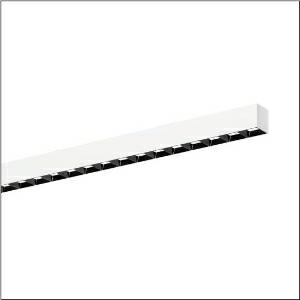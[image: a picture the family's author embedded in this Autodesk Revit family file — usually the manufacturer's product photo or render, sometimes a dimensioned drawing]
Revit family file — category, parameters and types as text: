
# Revit family: silica_r__21_51mx21dc4awb_19b2
name_source: partatom
category: Lighting Fixtures
units: mm (PartAtom-declared; Revit-internal decimal feet)

## family parameters
Cut with Voids When Loaded = No
Host = Face
Light Source = No
Part Type = Normal
Room Calculation Point = No
Round Connector Dimension = Use Diameter
Shared = No

## types (1)
- --- (1 x LED, 10800 lm, 64.8 W, 4000K)
    Apparent Load = 65 VA
    CIE Flux Codes = 87 99 100 100 100
    Color Rendering = 80
    Color Temperature = 4000K
    Default Elevation = 1800 mm
    Description = Silica® 21, office luminaire, primary light control with darklight reflector, of PMMA, black, CAT 2 (L<= 3000cd/m²), light emission: direct distribution, primary light characteristic: symmetric, installation type: surface-mounted, LED, rated luminous flux: 10.800lm, luminous efficacy: 167lm/W, light colour: 840, colour temperature: 4000K, control gear: DALI 2, with terminal, 3+2-pole, max. 2.5mm², mains connection: 220..240V, AC, 50/60Hz, rated input power: 64.8W, luminaire housing, of aluminium, traffic white (RAL 9016), length: 3.004mm, width: 53mm, height: 53mm, protection rating (complete): IP20, insulation class (complete): insulation class I (protective earthing), certification: CE, permissible operating ambient temperature: 0..+35°C, standard: EN 50419, packaging unit: 1 piece
    Height = 53 mm
    Lamp = 1 x LED
    Lamp Light Flux = 10800 lm
    Lamp Power = 64.8 W
    Lamp count = 1
    Length = 3004 mm
    Luminous efficacy = 167 lm/W
    Manufacturer = Siteco
    ModVariant = No
    Model = 51MX21DC4AWB
    Mounting Place = Ceiling
    Mounting Type = Surface mounted
    Number of Poles = 1
    OnlyDefault = Yes
    Power Factor = 1
    Product Name = Silica® 21
    Product group = office luminaire | ceiling mounted
    ProductGroupID = 303
    Protection Class = Protection class I
    Protection Degree = IP 20
    RLX_Detail_Level = 1
    RLX_Emergency_Light_Flux = 0 lm
    RLX_Emergency_Type = 0
    RLX_Emergency_Type_DB = No
    RlxData = <blob elided: 61313 chars, md5=3e0e4da8>
    Socket = socket
    Standby Power = 0 W
    System Light Flux = 10800 lm
    System Power = 65 W
    Type Comments = factory setting: luminous flux: 100 % | dim-lin: 254 | 367 mA
    Type Image = l_1335873.jpg
    URL = http://relux.com
    VarID = @adj_145395
    Voltage = 0 V
    Weight = 0.00 kg
    Width = 53 mm

## geometry (parser evidence)
native form markers: Blend x4, Sweep x11
no freeform markers — native parametric forms only
